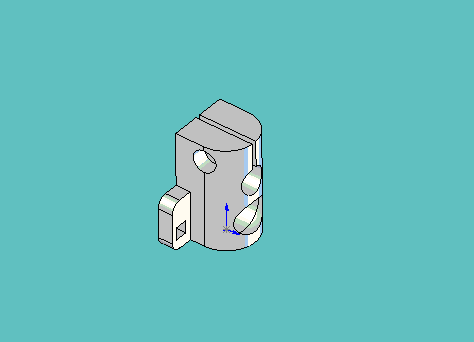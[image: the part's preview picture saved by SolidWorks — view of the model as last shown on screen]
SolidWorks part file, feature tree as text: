
SOLIDWORKS PART (.sldprt)
format: sldprt  version: not decoded by parser v0  size: 802,304 bytes
history: native  units: mm
features: sketch x10, cut_extrude x7, extrude x2, material x1, revolve x1, boolean_combine x1, plane x1, fillet x1 (+11 scaffold rows collapsed)
feature tree (35):
  scaffold x11  (default folders/planes/origin — collapsed)
  material  "Material <not specified>"
  sketch  "Sketch1"  dims[D1=19.05mm]
  extrude  "Extrude1"  Depth=33.3375mm
  sketch  "Sketch2"  dims[c1.D1=3.4544mm c1.D2=2.159mm c1.D6=2.159mm c1.D7=3.4544mm c1.D3=8.7376mm c1.D4=28.3464mm c2.D3=8.7376mm c2.D4=28.3464mm c2.D5=8.7376mm c2.D8=28.3464mm]
  cut_extrude  "Cut-Extrude1"  [1 undecoded]
  sketch  "Sketch3"  dims[c1.D4=12.7mm c1.D1=8.7376mm c1.D2=12.7mm c1.D3=6.35mm c1.D5=7.62mm c1.D6=5.1562mm c2.D2=~0.79375mm c2.D5=4.7625mm]
  revolve  "Revolve1"  Angle=360deg
  boolean_combine  "Combine1"
  sketch  "Sketch4"  dims[D1=8.5852mm D2=20.6502mm]
  cut_extrude  "Cut-Extrude2"  [1 undecoded]
  sketch  "Sketch5"  dims[D1=4.3688mm]
  cut_extrude  "Cut-Extrude3"  [1 undecoded]
  plane  "Plane1"  Offset=12.7mm
  sketch  "Sketch6"  dims[D1=~7.540625mm]
  cut_extrude  "Cut-Extrude4"  Depth=7.9375mm
  sketch  "Sketch7"  dims[D1=~0.79375mm D2=~0.79375mm]
  cut_extrude  "Cut-Extrude5"  Depth=12.7mm
  sketch  "Sketch11"  dims[D1=19.05mm D2=19.05mm D3=25.4mm D4=16.002mm]
  extrude  "Extrude2"  Depth=4.7625mm
  fillet  "Fillet1"  Radius=3.175mm
  sketch  "Sketch8"  dims[c1.D1=2.159mm c1.D2=~3.96875mm c1.D5=2.159mm c1.D3=15.24mm c1.D4=15.24mm c2.D5=3.175mm c2.D6=3.175mm c3.D5=3.175mm c3.D6=12.7mm c3.D7=~3.96875mm]
  cut_extrude  "Cut-Extrude6"  Depth=4.7625mm
  sketch  "Sketch10"  dims[D1=2.159mm]
  cut_extrude  "Cut-Extrude7"  [1 undecoded]
decode coverage: 17 of 22 modeling features carry decoded parameters
note: ~ marks probable driven/reference dimensions
note: 4 parameter values undecoded
summary: no parameter record found for 4 features
note: suppression state not decoded; provenance and decode notes live in map.json
